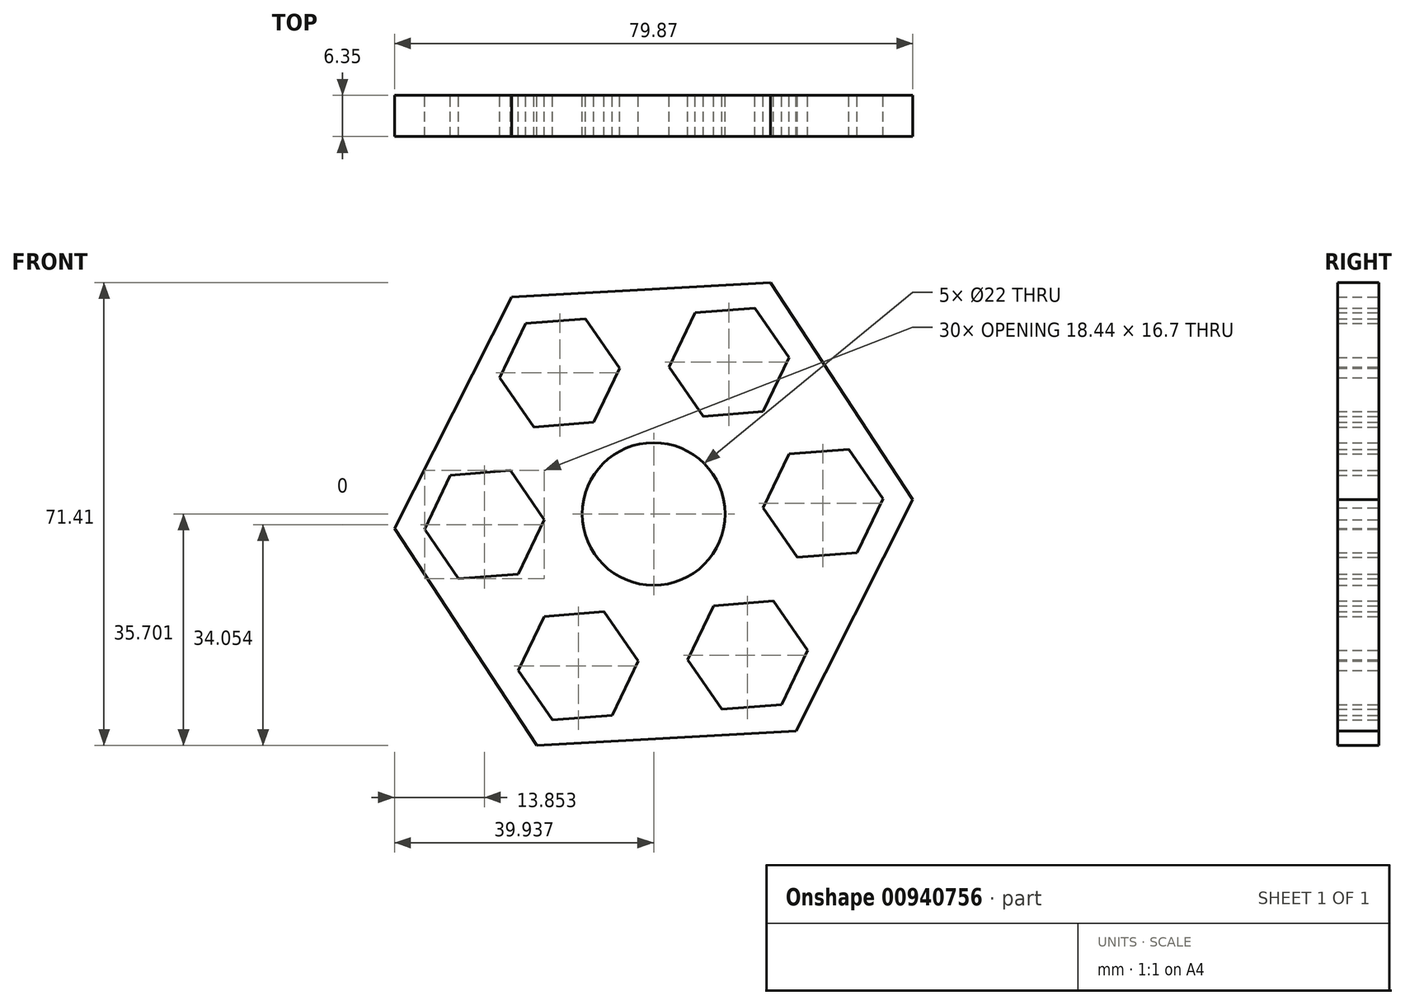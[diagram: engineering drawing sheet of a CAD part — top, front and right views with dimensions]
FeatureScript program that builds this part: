
annotation { "Feature Type Name" : "Feature", "Feature Type Description" : "" }
export const myFeature = defineFeature(function(context is Context, id is Id, definition is map)
    precondition{}
    {
        {
            var Q0;
            Q0=qCreatedBy(makeId("Front.planeOp"),FACE);
            var sketch = newSketch(context, id + "F0", { "sketchPlane" : qUnion([Q0])});
            skLineSegment(sketch, "E0.0", {"start": v(-175.76, 51.7) * mm, "end": v(-193.79, 16) * mm});
            skLineSegment(sketch, "E0.1", {"start": v(-193.79, 16) * mm, "end": v(-233.72, 13.77) * mm});
            skLineSegment(sketch, "E0.2", {"start": v(-233.72, 13.77) * mm, "end": v(-255.63, 47.23) * mm});
            skLineSegment(sketch, "E0.3", {"start": v(-255.63, 47.23) * mm, "end": v(-237.6, 82.94) * mm});
            skLineSegment(sketch, "E0.4", {"start": v(-237.6, 82.94) * mm, "end": v(-197.66, 85.18) * mm});
            skLineSegment(sketch, "E0.5", {"start": v(-197.66, 85.18) * mm, "end": v(-175.76, 51.7) * mm});
            skCircle(sketch, "E1.cCircle", {"center": v(-227.3, 26.06) * mm, "radius": 8.01 * mm});
            skLineSegment(sketch, "E1.0", {"start": v(-218.09, 26.78) * mm, "end": v(-222.07, 18.43) * mm});
            skLineSegment(sketch, "E1.1", {"start": v(-222.07, 18.43) * mm, "end": v(-231.3, 17.71) * mm});
            skLineSegment(sketch, "E1.2", {"start": v(-231.3, 17.71) * mm, "end": v(-236.53, 25.34) * mm});
            skLineSegment(sketch, "E1.3", {"start": v(-236.53, 25.34) * mm, "end": v(-232.55, 33.68) * mm});
            skLineSegment(sketch, "E1.4", {"start": v(-232.55, 33.68) * mm, "end": v(-223.32, 34.4) * mm});
            skLineSegment(sketch, "E1.5", {"start": v(-223.32, 34.4) * mm, "end": v(-218.09, 26.78) * mm});
            skPoint(sketch, "E1.0.midPoint", {"position": v(-220.08, 22.6) * mm});
            skLineSegment(sketch, "E2", {"start": v(-223.31, 34.39) * mm, "end": v(-223.86, 33.3) * mm, "construction": true});
            skPoint(sketch, "E3", {"position": v(-215.7, 49.47) * mm});
            skLineSegment(sketch, "E4.trimOffspring", {"start": v(-231.08, 19) * mm, "end": v(-231.55, 18.08) * mm, "construction": true});
            skLineSegment(sketch, "E5.1.0", {"start": v(-195.99, 20.08) * mm, "end": v(-205.2, 19.36) * mm});
            skCircle(sketch, "E5.1.1", {"center": v(-201.22, 27.7) * mm, "radius": 8.01 * mm});
            skLineSegment(sketch, "E5.1.2", {"start": v(-205.2, 19.36) * mm, "end": v(-210.45, 26.98) * mm});
            skLineSegment(sketch, "E5.1.3", {"start": v(-210.45, 26.98) * mm, "end": v(-206.46, 35.33) * mm});
            skLineSegment(sketch, "E5.1.4", {"start": v(-206.46, 35.33) * mm, "end": v(-197.24, 36.05) * mm});
            skLineSegment(sketch, "E5.1.5", {"start": v(-197.24, 36.05) * mm, "end": v(-192, 28.43) * mm});
            skLineSegment(sketch, "E5.1.6", {"start": v(-192, 28.43) * mm, "end": v(-195.99, 20.08) * mm});
            skLineSegment(sketch, "E5.2.0", {"start": v(-180.39, 51.84) * mm, "end": v(-184.37, 43.5) * mm});
            skCircle(sketch, "E5.2.1", {"center": v(-189.6, 51.12) * mm, "radius": 8.01 * mm});
            skLineSegment(sketch, "E5.2.2", {"start": v(-184.37, 43.5) * mm, "end": v(-193.6, 42.77) * mm});
            skLineSegment(sketch, "E5.2.3", {"start": v(-193.6, 42.77) * mm, "end": v(-198.83, 50.4) * mm});
            skLineSegment(sketch, "E5.2.4", {"start": v(-198.83, 50.4) * mm, "end": v(-194.85, 58.74) * mm});
            skLineSegment(sketch, "E5.2.5", {"start": v(-194.85, 58.74) * mm, "end": v(-185.62, 59.47) * mm});
            skLineSegment(sketch, "E5.2.6", {"start": v(-185.62, 59.47) * mm, "end": v(-180.39, 51.84) * mm});
            skLineSegment(sketch, "E5.3.0", {"start": v(-200.1, 81.23) * mm, "end": v(-194.86, 73.6) * mm});
            skCircle(sketch, "E5.3.1", {"center": v(-204.08, 72.88) * mm, "radius": 8.01 * mm});
            skLineSegment(sketch, "E5.3.2", {"start": v(-194.86, 73.6) * mm, "end": v(-198.84, 65.26) * mm});
            skLineSegment(sketch, "E5.3.3", {"start": v(-198.84, 65.26) * mm, "end": v(-208.06, 64.54) * mm});
            skLineSegment(sketch, "E5.3.4", {"start": v(-208.06, 64.54) * mm, "end": v(-213.3, 72.16) * mm});
            skLineSegment(sketch, "E5.3.5", {"start": v(-213.3, 72.16) * mm, "end": v(-209.31, 80.5) * mm});
            skLineSegment(sketch, "E5.3.6", {"start": v(-209.31, 80.5) * mm, "end": v(-200.1, 81.23) * mm});
            skLineSegment(sketch, "E5.4.0", {"start": v(-235.4, 78.86) * mm, "end": v(-226.18, 79.59) * mm});
            skCircle(sketch, "E5.4.1", {"center": v(-230.16, 71.24) * mm, "radius": 8.01 * mm});
            skLineSegment(sketch, "E5.4.2", {"start": v(-226.18, 79.59) * mm, "end": v(-220.94, 71.96) * mm});
            skLineSegment(sketch, "E5.4.3", {"start": v(-220.94, 71.96) * mm, "end": v(-224.92, 63.61) * mm});
            skLineSegment(sketch, "E5.4.4", {"start": v(-224.92, 63.61) * mm, "end": v(-234.15, 62.89) * mm});
            skLineSegment(sketch, "E5.4.5", {"start": v(-234.15, 62.89) * mm, "end": v(-239.38, 70.51) * mm});
            skLineSegment(sketch, "E5.4.6", {"start": v(-239.38, 70.51) * mm, "end": v(-235.4, 78.86) * mm});
            skLineSegment(sketch, "E5.5.0", {"start": v(-251, 47.1) * mm, "end": v(-247.01, 55.45) * mm});
            skCircle(sketch, "E5.5.1", {"center": v(-241.78, 47.82) * mm, "radius": 8.01 * mm});
            skLineSegment(sketch, "E5.5.2", {"start": v(-247.01, 55.45) * mm, "end": v(-237.8, 56.17) * mm});
            skLineSegment(sketch, "E5.5.3", {"start": v(-237.8, 56.17) * mm, "end": v(-232.55, 48.55) * mm});
            skLineSegment(sketch, "E5.5.4", {"start": v(-232.55, 48.55) * mm, "end": v(-236.54, 40.2) * mm});
            skLineSegment(sketch, "E5.5.5", {"start": v(-236.54, 40.2) * mm, "end": v(-245.76, 39.48) * mm});
            skLineSegment(sketch, "E5.5.6", {"start": v(-245.76, 39.48) * mm, "end": v(-251, 47.1) * mm});
            skCircle(sketch, "E6", {"center": v(-215.7, 49.47) * mm, "radius": 11 * mm});
            skSolve(sketch);
        }
        {
            var Q0;
            Q0 = qSketchRegion(id + "F0", true);
            extrude(context, id + "F1", {"entities" : qUnion([Q0]), "depth" : 6.35 * mm, "offsetDistance" : 25 * mm});
        }
    });
